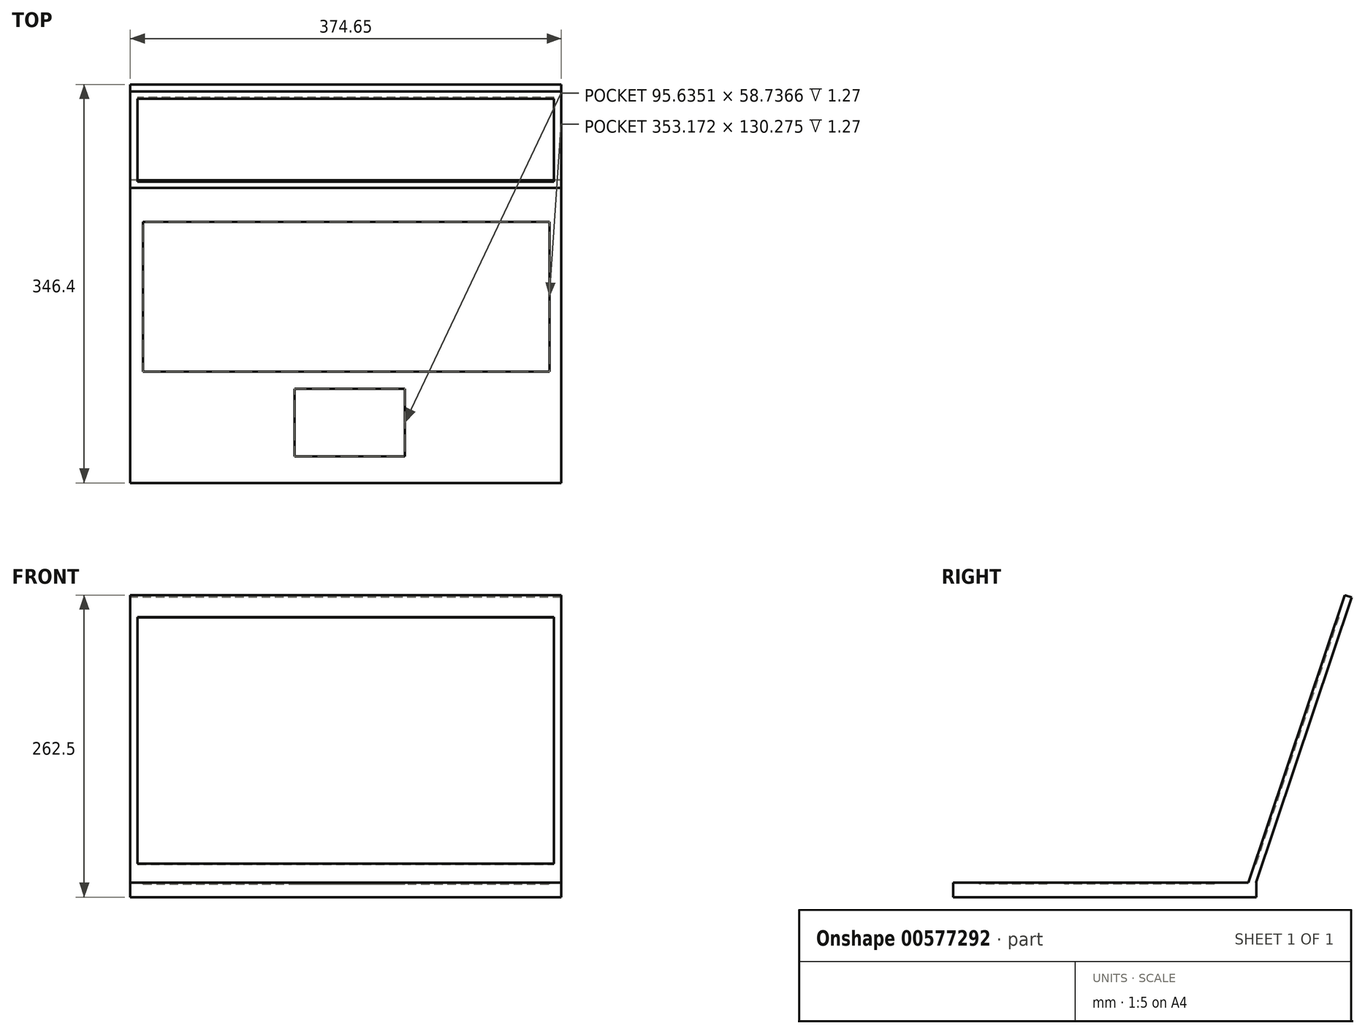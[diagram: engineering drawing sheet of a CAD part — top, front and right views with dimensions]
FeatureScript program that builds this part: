
annotation { "Feature Type Name" : "Feature", "Feature Type Description" : "" }
export const myFeature = defineFeature(function(context is Context, id is Id, definition is map)
    precondition{}
    {
        {
            var Q0;
            Q0=qCreatedBy(makeId("Right.planeOp"),FACE);
            var sketch = newSketch(context, id + "F0", { "sketchPlane" : qUnion([Q0])});
            skLineSegment(sketch, "E0", {"start": v(0, 0) * mm, "end": v(0, -12.7) * mm});
            skLineSegment(sketch, "E1", {"start": v(0, -12.7) * mm, "end": v(263.53, -12.7) * mm});
            skLineSegment(sketch, "E2", {"start": v(263.53, -12.7) * mm, "end": v(263.53, 0) * mm});
            skLineSegment(sketch, "E3", {"start": v(263.53, 0) * mm, "end": v(0, 0) * mm});
            skLineSegment(sketch, "E4", {"start": v(256.43, 0) * mm, "end": v(340.38, 249.8) * mm});
            skLineSegment(sketch, "E5", {"start": v(340.38, 249.8) * mm, "end": v(346.4, 247.77) * mm});
            skLineSegment(sketch, "E6", {"start": v(346.4, 247.77) * mm, "end": v(261, -6.35) * mm});
            skPoint(sketch, "E6.endSnap0", {"position": v(263.53, -6.35) * mm});
            skSolve(sketch);
        }
        {
            var Q0;
            Q0 = qSketchRegion(id + "F0", true);
            extrude(context, id + "F1", {"entities" : qUnion([Q0]), "depth" : 374.65 * mm, "offsetDistance" : 25.4 * mm});
        }
        {
            var Q0;
            Q0=makeQuery(id+"F1.opExtrude","SWEPT_FACE",FACE,{"disambiguationData":[OSD([sQuery(id+"F0.wireOp",EDGE,"E4")])]});
            var sketch = newSketch(context, id + "F2", { "sketchPlane" : qUnion([Q0])});
            skLineSegment(sketch, "E7.0", {"start": v(6.35, 338.86) * mm, "end": v(6.35, 88.04) * mm});
            skLineSegment(sketch, "E7.1", {"start": v(368.3, 338.86) * mm, "end": v(6.35, 338.86) * mm});
            skLineSegment(sketch, "E7.2", {"start": v(368.3, 88.04) * mm, "end": v(368.3, 338.86) * mm});
            skLineSegment(sketch, "E7.3", {"start": v(6.35, 88.04) * mm, "end": v(368.3, 88.04) * mm});
            skSolve(sketch);
        }
        {
            var Q0;
            Q0 = qSketchRegion(id + "F2", true);
            extrude(context, id + "F3", {"entities" : qUnion([Q0]), "operationType" : NewBodyOperationType.REMOVE, "oppositeDirection" : true, "depth" : 1.27 * mm, "offsetDistance" : 25.4 * mm});
        }
        {
            var Q0;
            {var subQ0=sQuery(id+"F0.wireOp",EDGE,"E3");Q0=makeQuery(id+"F1.opExtrude","SWEPT_FACE",FACE,{"disambiguationData":[OSD([subQ0]),TDD([makeQuery(id+"F0.imprint","IMPRINT",EDGE,{"disambiguationData":[TD([[makeQuery(id+"F0.imprint","INTERSECT",VERTEX,{"derivedFrom":[sQuery(id+"F0.wireOp",EDGE,"E0"),subQ0]}),1.0]])],"derivedFrom":subQ0})])]});}
            var sketch = newSketch(context, id + "F4", { "sketchPlane" : qUnion([Q0])});
            skLineSegment(sketch, "E8.bottom", {"start": v(11.12, 227.04) * mm, "end": v(364.29, 227.04) * mm});
            skLineSegment(sketch, "E8.top", {"start": v(11.12, 96.76) * mm, "end": v(364.29, 96.76) * mm});
            skLineSegment(sketch, "E8.left", {"start": v(11.12, 227.04) * mm, "end": v(11.12, 96.76) * mm});
            skLineSegment(sketch, "E8.right", {"start": v(364.29, 227.04) * mm, "end": v(364.29, 96.76) * mm});
            skLineSegment(sketch, "E9.bottom", {"start": v(142.9, 81.7) * mm, "end": v(238.53, 81.7) * mm});
            skLineSegment(sketch, "E9.top", {"start": v(142.9, 22.97) * mm, "end": v(238.53, 22.97) * mm});
            skLineSegment(sketch, "E9.left", {"start": v(142.9, 81.7) * mm, "end": v(142.9, 22.97) * mm});
            skLineSegment(sketch, "E9.right", {"start": v(238.53, 81.7) * mm, "end": v(238.53, 22.97) * mm});
            skSolve(sketch);
        }
        {
            var Q0;
            Q0 = qSketchRegion(id + "F4", true);
            extrude(context, id + "F5", {"entities" : qUnion([Q0]), "operationType" : NewBodyOperationType.REMOVE, "oppositeDirection" : true, "depth" : 1.27 * mm, "offsetDistance" : 25.4 * mm});
        }
        {
            var Q0;
            Q0=makeQuery(id+"F3.boolean.opBoolean","COPY",FACE,{"derivedFrom":makeQuery(id+"F3.opExtrude","CAP_FACE",FACE,{"disambiguationData":[OSD([sQuery(id+"F2.wireOp",EDGE,"E7.0"),sQuery(id+"F2.wireOp",EDGE,"E7.1"),sQuery(id+"F2.wireOp",EDGE,"E7.2"),sQuery(id+"F2.wireOp",EDGE,"E7.3")])],"isStart":false})});
            var sketch = newSketch(context, id + "F6", { "sketchPlane" : qUnion([Q0])});
            skLineSegment(sketch, "E10", {"start": v(368.3, 325.23) * mm, "end": v(6.35, 325.23) * mm});
            skLineSegment(sketch, "E11", {"start": v(6.35, 98.84) * mm, "end": v(368.3, 98.84) * mm});
            skSolve(sketch);
        }
        {
            var Q0;
            Q0 = qSketchRegion(id + "F6", true);
            var Q1;
            {var subQ0=sQuery(id+"F6.wireOp",EDGE,"E10");Q1=makeQuery(id+"F6.imprint","IMPRINT",FACE,{"disambiguationData":[TD([[makeQuery(id+"F6.imprint","IMPRINT",EDGE,{"derivedFrom":subQ0}),-1.0]])]});}
            var Q2;
            {var subQ0=sQuery(id+"F6.wireOp",EDGE,"E11");Q2=makeQuery(id+"F6.imprint","IMPRINT",FACE,{"disambiguationData":[TD([[makeQuery(id+"F6.imprint","IMPRINT",EDGE,{"derivedFrom":subQ0}),-1.0]])]});}
            var Q3;
            Q3=makeQuery(id+"F1.opExtrude","SWEPT_FACE",FACE,{"disambiguationData":[OSD([sQuery(id+"F0.wireOp",EDGE,"E4")])]});
            extrude(context, id + "F7", {"entities" : qUnion([Q0, Q1, Q2]), "operationType" : NewBodyOperationType.ADD, "endBound" : BoundingType.UP_TO_SURFACE, "depth" : 25.4 * mm, "endBoundEntityFace" : qUnion([Q3]), "offsetDistance" : 25.4 * mm});
        }
    });
